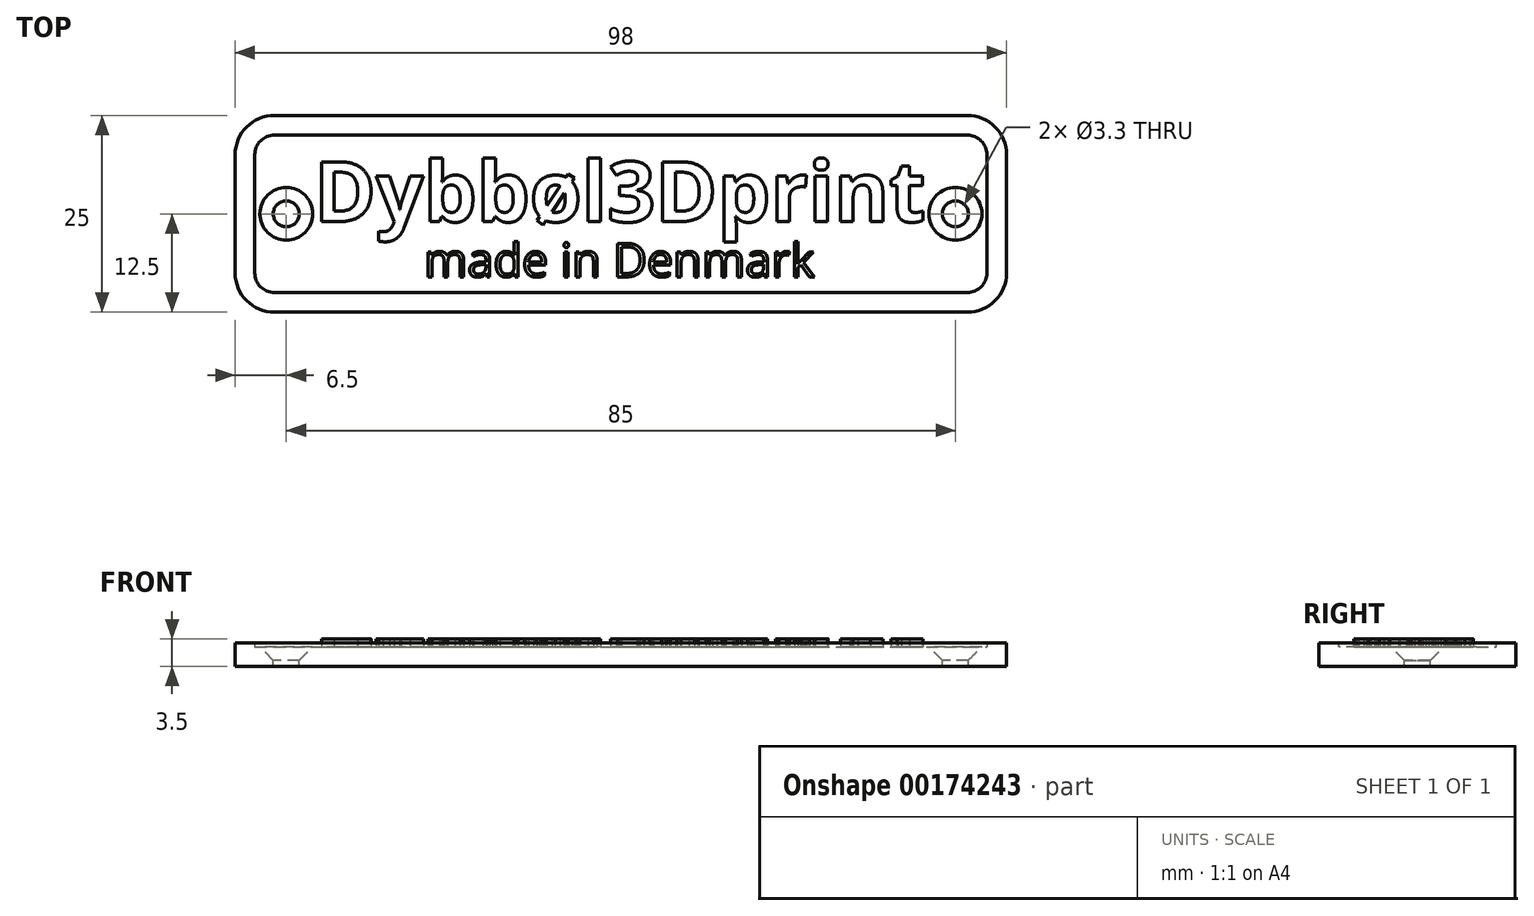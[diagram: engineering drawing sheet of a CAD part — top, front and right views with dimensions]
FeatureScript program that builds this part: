
annotation { "Feature Type Name" : "Feature", "Feature Type Description" : "" }
export const myFeature = defineFeature(function(context is Context, id is Id, definition is map)
    precondition{}
    {
        {
            var Q0;
            Q0=qCreatedBy(makeId("Top.planeOp"),FACE);
            var sketch = newSketch(context, id + "F0", { "sketchPlane" : qUnion([Q0])});
            skLineSegment(sketch, "E0.bottom", {"start": v(-49, 12.5) * mm, "end": v(49, 12.5) * mm});
            skLineSegment(sketch, "E0.top", {"start": v(-49, -12.5) * mm, "end": v(49, -12.5) * mm});
            skLineSegment(sketch, "E0.left", {"start": v(-49, 12.5) * mm, "end": v(-49, -12.5) * mm});
            skLineSegment(sketch, "E0.right", {"start": v(49, 12.5) * mm, "end": v(49, -12.5) * mm});
            skSolve(sketch);
        }
        {
            var Q0;
            Q0 = qSketchRegion(id + "F0", true);
            extrude(context, id + "F1", {"entities" : qUnion([Q0]), "depth" : 3 * mm});
        }
        {
            var Q0;
            Q0=makeQuery(id+"F1.opExtrude","SWEPT_EDGE",EDGE,{"disambiguationData":[OSD([sQuery(id+"F0.wireOp",EDGE,"E0.top"),sQuery(id+"F0.wireOp",EDGE,"E0.left")])]});
            var Q1;
            Q1=makeQuery(id+"F1.opExtrude","SWEPT_EDGE",EDGE,{"disambiguationData":[OSD([sQuery(id+"F0.wireOp",EDGE,"E0.top"),sQuery(id+"F0.wireOp",EDGE,"E0.right")])]});
            var Q2;
            Q2=makeQuery(id+"F1.opExtrude","SWEPT_EDGE",EDGE,{"disambiguationData":[OSD([sQuery(id+"F0.wireOp",EDGE,"E0.bottom"),sQuery(id+"F0.wireOp",EDGE,"E0.right")])]});
            var Q3;
            Q3=makeQuery(id+"F1.opExtrude","SWEPT_EDGE",EDGE,{"disambiguationData":[OSD([sQuery(id+"F0.wireOp",EDGE,"E0.bottom"),sQuery(id+"F0.wireOp",EDGE,"E0.left")])]});
            fillet(context, id + "F2", {"entities" : qUnion([Q0, Q1, Q2, Q3]), "radius" : 5 * mm, "tangentPropagation" : true, "allowEdgeOverflow" : false});
        }
        {
            var Q0;
            Q0=makeQuery(id+"F1.opExtrude","CAP_FACE",FACE,{"disambiguationData":[OSD([sQuery(id+"F0.wireOp",EDGE,"E0.bottom"),sQuery(id+"F0.wireOp",EDGE,"E0.top"),sQuery(id+"F0.wireOp",EDGE,"E0.left"),sQuery(id+"F0.wireOp",EDGE,"E0.right")])],"isStart":false});
            shell(context, id + "F3", {"entities" : qUnion([Q0]), "thickness" : 2.5 * mm});
        }
        {
            var Q0;
            Q0=makeQuery(id+"F3.opShell","OFFSET_FACE",FACE,{"disambiguationData":[OSD([sQuery(id+"F0.wireOp",EDGE,"E0.bottom"),sQuery(id+"F0.wireOp",EDGE,"E0.top"),sQuery(id+"F0.wireOp",EDGE,"E0.left"),sQuery(id+"F0.wireOp",EDGE,"E0.right")])]});
            var sketch = newSketch(context, id + "F4", { "sketchPlane" : qUnion([Q0])});
            skPoint(sketch, "E1", {"position": v(-42.5, 0) * mm});
            skPoint(sketch, "E2.MirrorP", {"position": v(42.5, 0) * mm});
            skSolve(sketch);
        }
        {
            var Q0;
            Q0=sQuery(id+"F4.wireOp",VERTEX,"E1");
            var Q1;
            Q1=sQuery(id+"F4.wireOp",VERTEX,"E2.MirrorP");
            var Q2;
            Q2=makeQuery(id+"F1.opExtrude","SWEPT_BODY",BODY,{"disambiguationData":[OSD([sQuery(id+"F0.wireOp",EDGE,"E0.bottom"),sQuery(id+"F0.wireOp",EDGE,"E0.top"),sQuery(id+"F0.wireOp",EDGE,"E0.left"),sQuery(id+"F0.wireOp",EDGE,"E0.right")])]});
            hole(context, id + "F5", {"style" : HoleStyle.C_SINK, "endStyle" : HoleEndStyle.THROUGH, "standardTappedOrClearance" : lookupTablePath({ "standard" : "ISO", "fit" : "Normal", "size" : "M3", "type" : "Clearance" }), "standardBlindInLast" : lookupTablePath({ "fit" : "Standard", "standard" : "ISO", "size" : "M3", "type" : "Clearance" }), "holeDiameter" : 3.3 * mm, "cSinkDiameter" : 6.72 * mm, "cSinkAngle" : 90 * degree, "startFromSketch" : true, "locations" : qUnion([Q0, Q1]), "scope" : qUnion([Q2]), "isTappedThrough" : true});
        }
        {
            var Q0;
            Q0=makeQuery(id+"F3.opShell","OFFSET_FACE",FACE,{"disambiguationData":[OSD([sQuery(id+"F0.wireOp",EDGE,"E0.bottom"),sQuery(id+"F0.wireOp",EDGE,"E0.top"),sQuery(id+"F0.wireOp",EDGE,"E0.left"),sQuery(id+"F0.wireOp",EDGE,"E0.right")])]});
            var sketch = newSketch(context, id + "F6", { "sketchPlane" : qUnion([Q0])});
            skText(sketch, "E3", { "text": "Dybbøl3Dprint", "fontName": "OpenSans-Bold.ttf"});
            skText(sketch, "E4", { "text": "made in Denmark", "fontName": "OpenSans-Regular.ttf"});
            const initialGuessF6  = {"E3": [-0.039, -0.001, 1, 0, 0.00767], "E4": [-0.025, -0.008, 1, 0, 0.00427]};
            skSetInitialGuess(sketch, initialGuessF6);
            skSolve(sketch);
        }
        {
            var Q0;
            Q0 = qSketchRegion(id + "F6", true);
            extrude(context, id + "F7", {"entities" : qUnion([Q0]), "operationType" : NewBodyOperationType.ADD, "depth" : 1 * mm});
        }
    });
